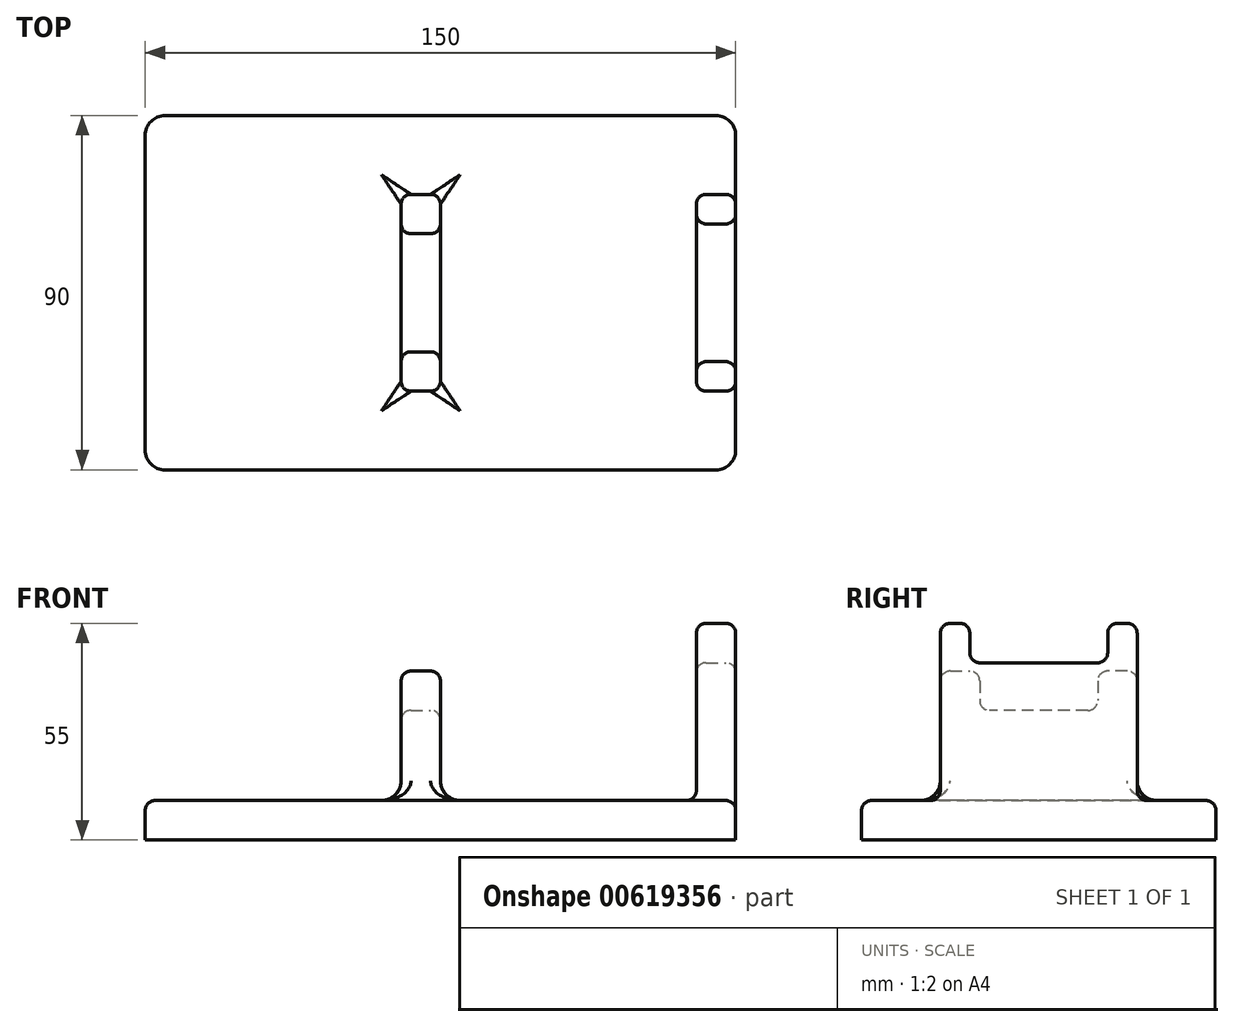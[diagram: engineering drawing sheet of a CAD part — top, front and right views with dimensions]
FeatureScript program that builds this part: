
annotation { "Feature Type Name" : "Feature", "Feature Type Description" : "" }
export const myFeature = defineFeature(function(context is Context, id is Id, definition is map)
    precondition{}
    {
        {
            var Q0;
            Q0=qCreatedBy(makeId("Top.planeOp"),FACE);
            var sketch = newSketch(context, id + "F0", { "sketchPlane" : qUnion([Q0])});
            skLineSegment(sketch, "E0.bottom", {"start": v(-70, 45) * mm, "end": v(70, 45) * mm});
            skLineSegment(sketch, "E0.top", {"start": v(-70, -45) * mm, "end": v(70, -45) * mm});
            skLineSegment(sketch, "E0.left", {"start": v(-75, 40) * mm, "end": v(-75, -40) * mm});
            skLineSegment(sketch, "E0.right", {"start": v(75, 40) * mm, "end": v(75, -40) * mm});
            skPoint(sketch, "E0.middle", {"position": v(0, 0) * mm});
            skPoint(sketch, "E1.visualSharp", {"position": v(-75, 45) * mm});
            skArc(sketch, "E1.filletArc", {"start": v(-70, 45) * mm, "mid": v(-73.54, 43.54) * mm, "end": v(-75, 40) * mm});
            skPoint(sketch, "E2.visualSharp", {"position": v(-75, -45) * mm});
            skArc(sketch, "E2.filletArc", {"start": v(-75, -40) * mm, "mid": v(-73.54, -43.54) * mm, "end": v(-70, -45) * mm});
            skPoint(sketch, "E3.visualSharp", {"position": v(75, -45) * mm});
            skArc(sketch, "E3.filletArc", {"start": v(70, -45) * mm, "mid": v(73.54, -43.54) * mm, "end": v(75, -40) * mm});
            skPoint(sketch, "E4.visualSharp", {"position": v(75, 45) * mm});
            skArc(sketch, "E4.filletArc", {"start": v(75, 40) * mm, "mid": v(73.54, 43.54) * mm, "end": v(70, 45) * mm});
            skSolve(sketch);
        }
        {
            var Q0;
            Q0 = qSketchRegion(id + "F0", true);
            extrude(context, id + "F1", {"entities" : qUnion([Q0]), "depth" : 10 * mm, "offsetDistance" : 25 * mm});
        }
        {
            var Q0;
            Q0=qCreatedBy(makeId("Right.planeOp"),FACE);
            var sketch = newSketch(context, id + "F2", { "sketchPlane" : qUnion([Q0])});
            skLineSegment(sketch, "E5", {"start": v(0, 0) * mm, "end": v(0, 45.87) * mm, "construction": true});
            skSolve(sketch);
        }
        {
            var Q0;
            Q0=makeQuery(id+"F1.opExtrude","SWEPT_FACE",FACE,{"disambiguationData":[OSD([sQuery(id+"F0.wireOp",EDGE,"E0.right")])]});
            var sketch = newSketch(context, id + "F3", { "sketchPlane" : qUnion([Q0])});
            skLineSegment(sketch, "E6", {"start": v(-25, 10) * mm, "end": v(-25, 55) * mm});
            skLineSegment(sketch, "E7", {"start": v(-25, 55) * mm, "end": v(-17.5, 55) * mm});
            skLineSegment(sketch, "E8", {"start": v(-17.5, 55) * mm, "end": v(-17.5, 45) * mm});
            skLineSegment(sketch, "E9", {"start": v(-17.5, 45) * mm, "end": v(0, 45) * mm});
            skLineSegment(sketch, "E10.MirrorCS", {"start": v(25, 10) * mm, "end": v(25, 55) * mm});
            skLineSegment(sketch, "E11.MirrorCS", {"start": v(25, 55) * mm, "end": v(17.5, 55) * mm});
            skLineSegment(sketch, "E12.MirrorCS", {"start": v(17.5, 55) * mm, "end": v(17.5, 45) * mm});
            skLineSegment(sketch, "E13.MirrorCS", {"start": v(17.5, 45) * mm, "end": v(0, 45) * mm});
            skSolve(sketch);
        }
        {
            var Q0;
            {var subQ0=sQuery(id+"F3.wireOp",EDGE,"E6");Q0=makeQuery(id+"F3.imprint","IMPRINT",FACE,{"disambiguationData":[TD([[makeQuery(id+"F3.imprint","IMPRINT",EDGE,{"derivedFrom":subQ0}),-1.0]])]});}
            extrude(context, id + "F4", {"entities" : qUnion([Q0]), "operationType" : NewBodyOperationType.ADD, "oppositeDirection" : true, "depth" : 10 * mm, "offsetDistance" : 25 * mm});
        }
        {
            var Q0;
            Q0=qCreatedBy(makeId("Right.planeOp"),FACE);
            var sketch = newSketch(context, id + "F5", { "sketchPlane" : qUnion([Q0])});
            skLineSegment(sketch, "E14", {"start": v(0, 7.9) * mm, "end": v(-25, 7.9) * mm});
            skLineSegment(sketch, "E15", {"start": v(-25, 7.9) * mm, "end": v(-25, 42.9) * mm});
            skLineSegment(sketch, "E16", {"start": v(-25, 42.9) * mm, "end": v(-15, 42.9) * mm});
            skLineSegment(sketch, "E17", {"start": v(-15, 42.9) * mm, "end": v(-15, 32.9) * mm});
            skLineSegment(sketch, "E18", {"start": v(-15, 32.9) * mm, "end": v(0, 32.9) * mm});
            skLineSegment(sketch, "E19.MirrorCS", {"start": v(25, 7.9) * mm, "end": v(25, 42.9) * mm});
            skLineSegment(sketch, "E20.MirrorCS", {"start": v(25, 42.9) * mm, "end": v(15, 42.9) * mm});
            skLineSegment(sketch, "E21.MirrorCS", {"start": v(15, 42.9) * mm, "end": v(15, 32.9) * mm});
            skLineSegment(sketch, "E22.MirrorCS", {"start": v(15, 32.9) * mm, "end": v(0, 32.9) * mm});
            skLineSegment(sketch, "E23.MirrorCS", {"start": v(0, 7.9) * mm, "end": v(25, 7.9) * mm});
            skSolve(sketch);
        }
        {
            var Q0;
            Q0=makeQuery(id+"F5.imprint","IMPRINT",FACE,{"disambiguationData":[TD([[makeQuery(id+"F5.imprint","IMPRINT",EDGE,{"derivedFrom":sQuery(id+"F5.wireOp",EDGE,"E14")}),-1.0]])]});
            extrude(context, id + "F6", {"entities" : qUnion([Q0]), "operationType" : NewBodyOperationType.ADD, "oppositeDirection" : true, "depth" : 10 * mm, "offsetDistance" : 25 * mm});
        }
        {
            var Q0;
            Q0=makeQuery(id+"F6.boolean.opBoolean","INTERSECT",EDGE,{"derivedFrom":[makeQuery(id+"F1.opExtrude","CAP_FACE",FACE,{"disambiguationData":[OSD([sQuery(id+"F0.wireOp",EDGE,"E0.bottom"),sQuery(id+"F0.wireOp",EDGE,"E0.top"),sQuery(id+"F0.wireOp",EDGE,"E0.left"),sQuery(id+"F0.wireOp",EDGE,"E0.right"),sQuery(id+"F0.wireOp",EDGE,"E1.filletArc"),sQuery(id+"F0.wireOp",EDGE,"E2.filletArc"),sQuery(id+"F0.wireOp",EDGE,"E3.filletArc"),sQuery(id+"F0.wireOp",EDGE,"E4.filletArc")])],"isStart":false}),makeQuery(id+"F6.opExtrude","CAP_FACE",FACE,{"disambiguationData":[OSD([sQuery(id+"F5.wireOp",EDGE,"E14"),sQuery(id+"F5.wireOp",EDGE,"E15"),sQuery(id+"F5.wireOp",EDGE,"E16"),sQuery(id+"F5.wireOp",EDGE,"E17"),sQuery(id+"F5.wireOp",EDGE,"E18"),sQuery(id+"F5.wireOp",EDGE,"E19.MirrorCS"),sQuery(id+"F5.wireOp",EDGE,"E20.MirrorCS"),sQuery(id+"F5.wireOp",EDGE,"E21.MirrorCS"),sQuery(id+"F5.wireOp",EDGE,"E22.MirrorCS"),sQuery(id+"F5.wireOp",EDGE,"E23.MirrorCS")])],"isStart":false})]});
            var Q1;
            Q1=makeQuery(id+"F6.boolean.opBoolean","INTERSECT",EDGE,{"derivedFrom":[makeQuery(id+"F1.opExtrude","CAP_FACE",FACE,{"disambiguationData":[OSD([sQuery(id+"F0.wireOp",EDGE,"E0.bottom"),sQuery(id+"F0.wireOp",EDGE,"E0.top"),sQuery(id+"F0.wireOp",EDGE,"E0.left"),sQuery(id+"F0.wireOp",EDGE,"E0.right"),sQuery(id+"F0.wireOp",EDGE,"E1.filletArc"),sQuery(id+"F0.wireOp",EDGE,"E2.filletArc"),sQuery(id+"F0.wireOp",EDGE,"E3.filletArc"),sQuery(id+"F0.wireOp",EDGE,"E4.filletArc")])],"isStart":false}),makeQuery(id+"F6.opExtrude","CAP_FACE",FACE,{"disambiguationData":[OSD([sQuery(id+"F5.wireOp",EDGE,"E14"),sQuery(id+"F5.wireOp",EDGE,"E15"),sQuery(id+"F5.wireOp",EDGE,"E16"),sQuery(id+"F5.wireOp",EDGE,"E17"),sQuery(id+"F5.wireOp",EDGE,"E18"),sQuery(id+"F5.wireOp",EDGE,"E19.MirrorCS"),sQuery(id+"F5.wireOp",EDGE,"E20.MirrorCS"),sQuery(id+"F5.wireOp",EDGE,"E21.MirrorCS"),sQuery(id+"F5.wireOp",EDGE,"E22.MirrorCS"),sQuery(id+"F5.wireOp",EDGE,"E23.MirrorCS")])],"isStart":true})]});
            var Q2;
            Q2=makeQuery(id+"F6.boolean.opBoolean","INTERSECT",EDGE,{"derivedFrom":[makeQuery(id+"F1.opExtrude","CAP_FACE",FACE,{"disambiguationData":[OSD([sQuery(id+"F0.wireOp",EDGE,"E0.bottom"),sQuery(id+"F0.wireOp",EDGE,"E0.top"),sQuery(id+"F0.wireOp",EDGE,"E0.left"),sQuery(id+"F0.wireOp",EDGE,"E0.right"),sQuery(id+"F0.wireOp",EDGE,"E1.filletArc"),sQuery(id+"F0.wireOp",EDGE,"E2.filletArc"),sQuery(id+"F0.wireOp",EDGE,"E3.filletArc"),sQuery(id+"F0.wireOp",EDGE,"E4.filletArc")])],"isStart":false}),makeQuery(id+"F6.opExtrude","SWEPT_FACE",FACE,{"disambiguationData":[OSD([sQuery(id+"F5.wireOp",EDGE,"E19.MirrorCS")])]})]});
            var Q3;
            Q3=makeQuery(id+"F6.boolean.opBoolean","INTERSECT",EDGE,{"derivedFrom":[makeQuery(id+"F1.opExtrude","CAP_FACE",FACE,{"disambiguationData":[OSD([sQuery(id+"F0.wireOp",EDGE,"E0.bottom"),sQuery(id+"F0.wireOp",EDGE,"E0.top"),sQuery(id+"F0.wireOp",EDGE,"E0.left"),sQuery(id+"F0.wireOp",EDGE,"E0.right"),sQuery(id+"F0.wireOp",EDGE,"E1.filletArc"),sQuery(id+"F0.wireOp",EDGE,"E2.filletArc"),sQuery(id+"F0.wireOp",EDGE,"E3.filletArc"),sQuery(id+"F0.wireOp",EDGE,"E4.filletArc")])],"isStart":false}),makeQuery(id+"F6.opExtrude","SWEPT_FACE",FACE,{"disambiguationData":[OSD([sQuery(id+"F5.wireOp",EDGE,"E15")])]})]});
            var Q4;
            Q4=makeQuery(id+"F4.opExtrude","SWEPT_EDGE",EDGE,{"disambiguationData":[OSD([sQuery(id+"F0.wireOp",EDGE,"E0.right"),sQuery(id+"F3.wireOp",EDGE,"E10.MirrorCS")])]});
            var Q5;
            Q5=makeQuery(id+"F4.opExtrude","CAP_EDGE",EDGE,{"disambiguationData":[OSD([sQuery(id+"F0.wireOp",EDGE,"E0.right")])],"isStart":false});
            var Q6;
            Q6=makeQuery(id+"F4.opExtrude","SWEPT_EDGE",EDGE,{"disambiguationData":[OSD([sQuery(id+"F0.wireOp",EDGE,"E0.right"),sQuery(id+"F3.wireOp",EDGE,"E6")])]});
            fillet(context, id + "F7", {"entities" : qUnion([Q0, Q1, Q2, Q3, Q4, Q5, Q6]), "radius" : 5 * mm, "tangentPropagation" : true, "allowEdgeOverflow" : false});
        }
        {
            var Q0;
            Q0=makeQuery(id+"F6.opExtrude","SWEPT_FACE",FACE,{"disambiguationData":[OSD([sQuery(id+"F5.wireOp",EDGE,"E17")])]});
            var Q1;
            Q1=makeQuery(id+"F6.opExtrude","SWEPT_FACE",FACE,{"disambiguationData":[OSD([sQuery(id+"F5.wireOp",EDGE,"E18"),sQuery(id+"F5.wireOp",EDGE,"E22.MirrorCS")])]});
            var Q2;
            Q2=makeQuery(id+"F6.opExtrude","SWEPT_FACE",FACE,{"disambiguationData":[OSD([sQuery(id+"F5.wireOp",EDGE,"E21.MirrorCS")])]});
            var Q3;
            Q3=makeQuery(id+"F6.opExtrude","SWEPT_FACE",FACE,{"disambiguationData":[OSD([sQuery(id+"F5.wireOp",EDGE,"E16")])]});
            var Q4;
            Q4=makeQuery(id+"F6.opExtrude","SWEPT_EDGE",EDGE,{"disambiguationData":[OSD([sQuery(id+"F5.wireOp",EDGE,"E19.MirrorCS"),sQuery(id+"F5.wireOp",EDGE,"E20.MirrorCS")])]});
            var Q5;
            Q5=makeQuery(id+"F4.opExtrude","SWEPT_FACE",FACE,{"disambiguationData":[OSD([sQuery(id+"F3.wireOp",EDGE,"E11.MirrorCS")])]});
            var Q6;
            Q6=makeQuery(id+"F4.opExtrude","SWEPT_FACE",FACE,{"disambiguationData":[OSD([sQuery(id+"F3.wireOp",EDGE,"E9"),sQuery(id+"F3.wireOp",EDGE,"E13.MirrorCS")])]});
            var Q7;
            Q7=makeQuery(id+"F4.opExtrude","SWEPT_FACE",FACE,{"disambiguationData":[OSD([sQuery(id+"F3.wireOp",EDGE,"E8")])]});
            var Q8;
            Q8=makeQuery(id+"F4.opExtrude","SWEPT_FACE",FACE,{"disambiguationData":[OSD([sQuery(id+"F3.wireOp",EDGE,"E12.MirrorCS")])]});
            var Q9;
            Q9=makeQuery(id+"F4.opExtrude","SWEPT_FACE",FACE,{"disambiguationData":[OSD([sQuery(id+"F3.wireOp",EDGE,"E7")])]});
            var Q10;
            Q10=makeQuery(id+"F6.opExtrude","SWEPT_FACE",FACE,{"disambiguationData":[OSD([sQuery(id+"F5.wireOp",EDGE,"E19.MirrorCS")])]});
            var Q11;
            Q11=makeQuery(id+"F4.opExtrude","SWEPT_FACE",FACE,{"disambiguationData":[OSD([sQuery(id+"F3.wireOp",EDGE,"E10.MirrorCS")])]});
            var Q12;
            Q12=makeQuery(id+"F1.opExtrude","CAP_FACE",FACE,{"disambiguationData":[OSD([sQuery(id+"F0.wireOp",EDGE,"E0.bottom"),sQuery(id+"F0.wireOp",EDGE,"E0.top"),sQuery(id+"F0.wireOp",EDGE,"E0.left"),sQuery(id+"F0.wireOp",EDGE,"E0.right"),sQuery(id+"F0.wireOp",EDGE,"E1.filletArc"),sQuery(id+"F0.wireOp",EDGE,"E2.filletArc"),sQuery(id+"F0.wireOp",EDGE,"E3.filletArc"),sQuery(id+"F0.wireOp",EDGE,"E4.filletArc")])],"isStart":false});
            var Q13;
            Q13=makeQuery(id+"F6.opExtrude","SWEPT_FACE",FACE,{"disambiguationData":[OSD([sQuery(id+"F5.wireOp",EDGE,"E15")])]});
            var Q14;
            Q14=makeQuery(id+"F4.opExtrude","SWEPT_FACE",FACE,{"disambiguationData":[OSD([sQuery(id+"F3.wireOp",EDGE,"E6")])]});
            var Q15;
            Q15=makeQuery(id+"F6.opExtrude","SWEPT_FACE",FACE,{"disambiguationData":[OSD([sQuery(id+"F5.wireOp",EDGE,"E20.MirrorCS")])]});
            fillet(context, id + "F8", {"entities" : qUnion([Q0, Q1, Q2, Q3, Q4, Q5, Q6, Q7, Q8, Q9, Q10, Q11, Q12, Q13, Q14, Q15]), "radius" : 2.5 * mm, "tangentPropagation" : true, "allowEdgeOverflow" : false});
        }
    });
